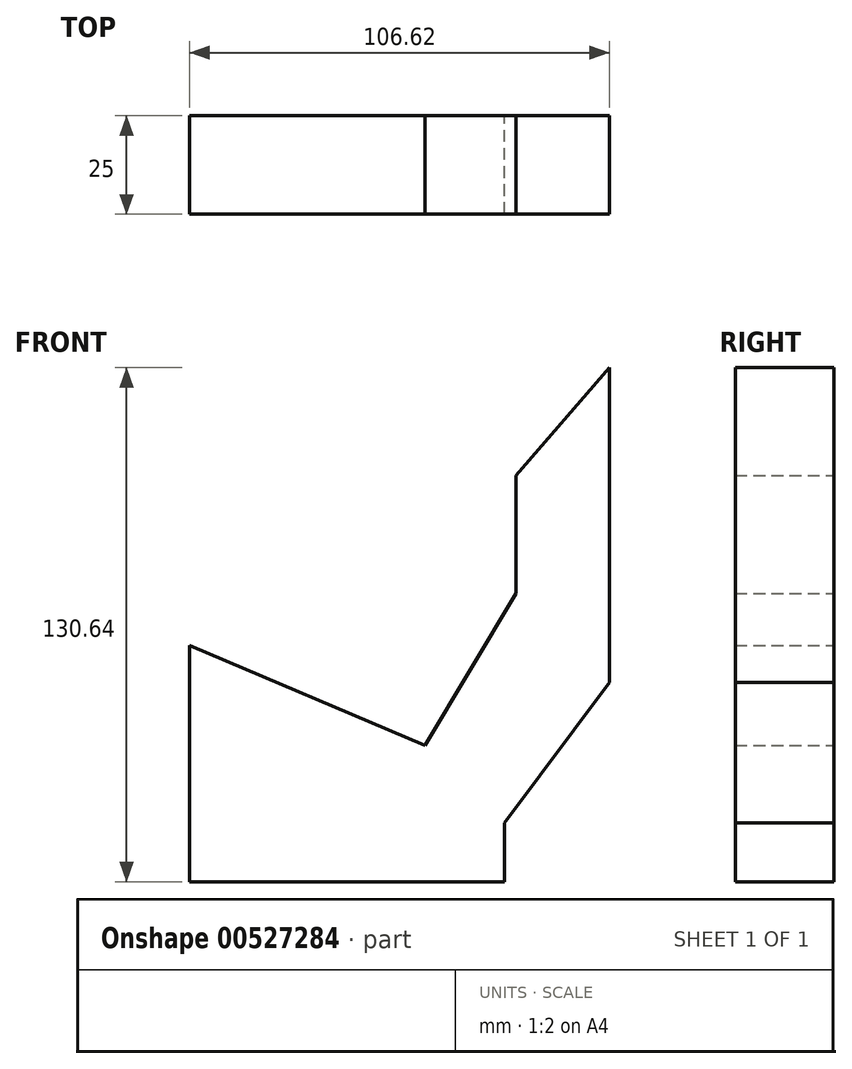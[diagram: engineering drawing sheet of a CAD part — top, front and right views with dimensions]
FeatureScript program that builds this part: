
annotation { "Feature Type Name" : "Feature", "Feature Type Description" : "" }
export const myFeature = defineFeature(function(context is Context, id is Id, definition is map)
    precondition{}
    {
        {
            var Q0;
            Q0=qCreatedBy(makeId("Front.planeOp"),FACE);
            var sketch = newSketch(context, id + "F0", { "sketchPlane" : qUnion([Q0])});
            skLineSegment(sketch, "E0", {"start": v(-34.82, 9.36) * mm, "end": v(-34.82, -50.64) * mm});
            skLineSegment(sketch, "E1", {"start": v(-34.82, -50.64) * mm, "end": v(45.18, -50.64) * mm});
            skLineSegment(sketch, "E2", {"start": v(45.18, -50.64) * mm, "end": v(45.18, -35.64) * mm});
            skLineSegment(sketch, "E3", {"start": v(45.18, -35.64) * mm, "end": v(71.8, 0) * mm});
            skLineSegment(sketch, "E4", {"start": v(71.8, 0) * mm, "end": v(71.8, 80) * mm});
            skLineSegment(sketch, "E5", {"start": v(71.8, 80) * mm, "end": v(48.01, 52.64) * mm});
            skLineSegment(sketch, "E6", {"start": v(48.01, 52.64) * mm, "end": v(48.01, 22.64) * mm});
            skLineSegment(sketch, "E7", {"start": v(48.01, 22.64) * mm, "end": v(25, -16.03) * mm});
            skLineSegment(sketch, "E8", {"start": v(-34.82, 9.36) * mm, "end": v(25, -16.03) * mm});
            skSolve(sketch);
        }
        {
            var Q0;
            Q0=makeQuery(id+"F0.imprint","IMPRINT",FACE,{"disambiguationData":[TD([[makeQuery(id+"F0.imprint","IMPRINT",EDGE,{"derivedFrom":sQuery(id+"F0.wireOp",EDGE,"E0")}),1.0]])]});
            extrude(context, id + "F1", {"entities" : qUnion([Q0]), "depth" : 25 * mm, "offsetDistance" : 25 * mm});
        }
    });
